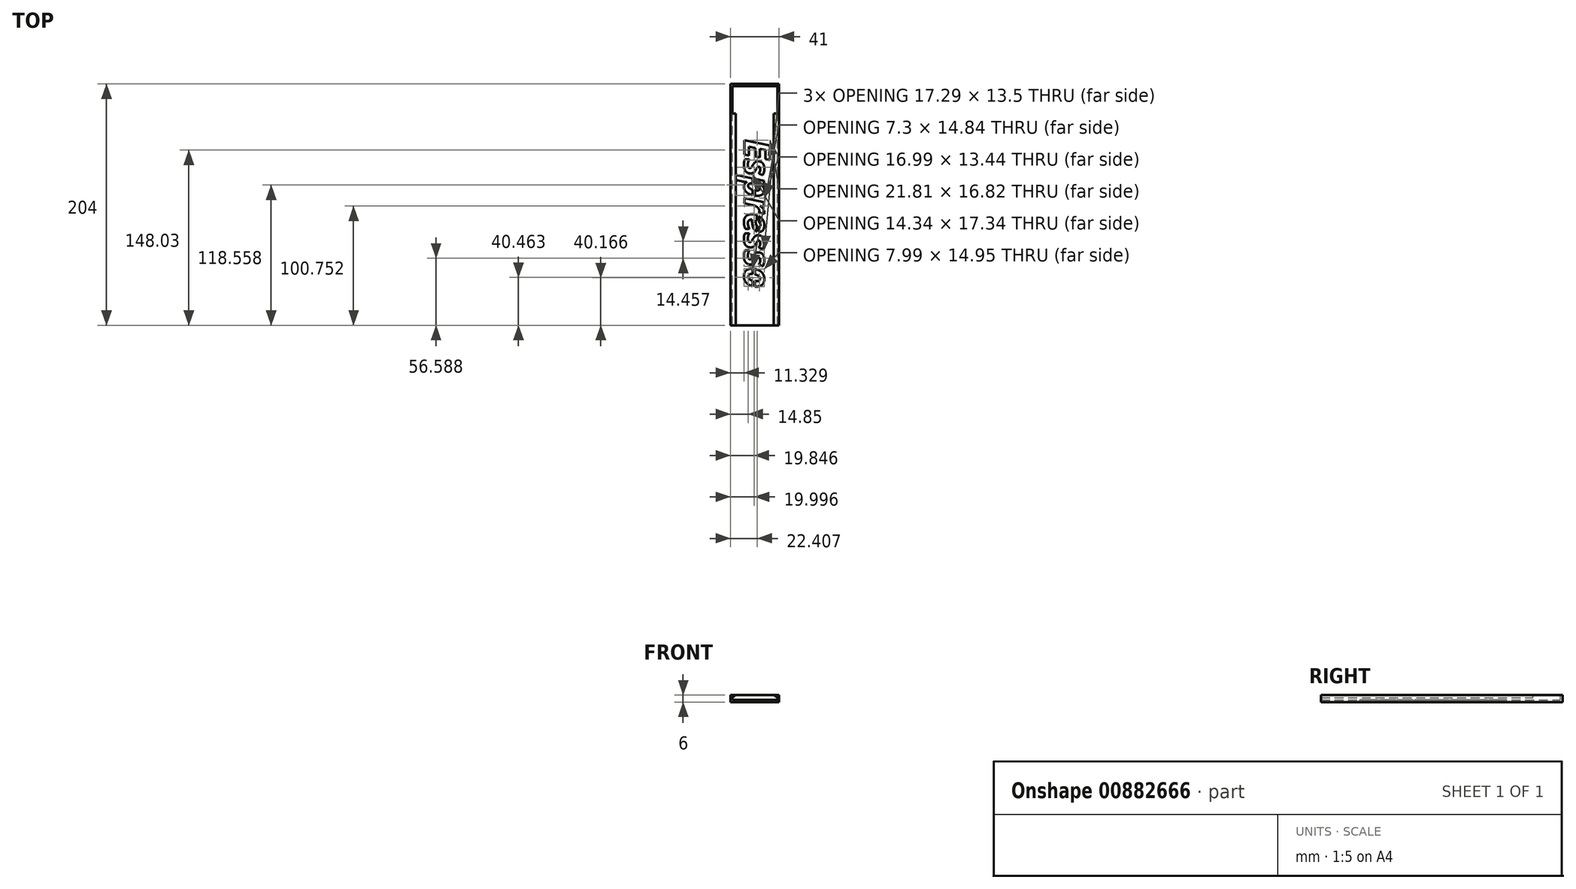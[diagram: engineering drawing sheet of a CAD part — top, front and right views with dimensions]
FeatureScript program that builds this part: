
annotation { "Feature Type Name" : "Feature", "Feature Type Description" : "" }
export const myFeature = defineFeature(function(context is Context, id is Id, definition is map)
    precondition{}
    {
        {
            var Q0;
            Q0=qCreatedBy(makeId("Front.planeOp"),FACE);
            var sketch = newSketch(context, id + "F0", { "sketchPlane" : qUnion([Q0])});
            skLineSegment(sketch, "E0", {"start": v(-20.5, 0) * mm, "end": v(20.5, 0) * mm});
            skLineSegment(sketch, "E1", {"start": v(20.5, 0) * mm, "end": v(20.5, 6) * mm});
            skLineSegment(sketch, "E2", {"start": v(20.5, 6) * mm, "end": v(16, 6) * mm});
            skLineSegment(sketch, "E3", {"start": v(19, 2) * mm, "end": v(-19, 2) * mm});
            skLineSegment(sketch, "E4", {"start": v(-16, 6) * mm, "end": v(-20.5, 6) * mm});
            skLineSegment(sketch, "E5", {"start": v(-20.5, 6) * mm, "end": v(-20.5, 0) * mm});
            skLineSegment(sketch, "E6", {"start": v(-16, 6) * mm, "end": v(16, 6) * mm});
            skLineSegment(sketch, "E7", {"start": v(16, 6) * mm, "end": v(19, 3.6) * mm});
            skLineSegment(sketch, "E8", {"start": v(19, 3.6) * mm, "end": v(19, 2) * mm});
            skLineSegment(sketch, "E9", {"start": v(-16, 6) * mm, "end": v(-19, 3.6) * mm});
            skLineSegment(sketch, "E10", {"start": v(-19, 3.6) * mm, "end": v(-19, 2) * mm});
            skSolve(sketch);
        }
        {
            var Q0;
            Q0=makeQuery(id+"F0.imprint","IMPRINT",FACE,{"disambiguationData":[TD([[makeQuery(id+"F0.imprint","IMPRINT",EDGE,{"derivedFrom":sQuery(id+"F0.wireOp",EDGE,"E0")}),1.0]])]});
            extrude(context, id + "F1", {"entities" : qUnion([Q0]), "depth" : 202 * mm, "offsetDistance" : 25 * mm});
        }
        {
            var Q0;
            Q0=qCreatedBy(makeId("Front.planeOp"),FACE);
            var sketch = newSketch(context, id + "F2", { "sketchPlane" : qUnion([Q0])});
            skLineSegment(sketch, "E11.bottom", {"start": v(20.5, 6) * mm, "end": v(-20.5, 6) * mm});
            skLineSegment(sketch, "E11.top", {"start": v(20.5, 0) * mm, "end": v(-20.5, 0) * mm});
            skLineSegment(sketch, "E11.left", {"start": v(20.5, 6) * mm, "end": v(20.5, 0) * mm});
            skLineSegment(sketch, "E11.right", {"start": v(-20.5, 6) * mm, "end": v(-20.5, 0) * mm});
            skSolve(sketch);
        }
        {
            var Q0;
            Q0=makeQuery(id+"F2.imprint","IMPRINT",FACE,{"disambiguationData":[TD([[makeQuery(id+"F2.imprint","IMPRINT",EDGE,{"derivedFrom":sQuery(id+"F2.wireOp",EDGE,"E11.bottom")}),1.0]])]});
            extrude(context, id + "F3", {"entities" : qUnion([Q0]), "operationType" : NewBodyOperationType.ADD, "oppositeDirection" : true, "depth" : 2 * mm, "offsetDistance" : 25 * mm});
        }
        {
            var Q0;
            Q0=makeQuery(id+"F3.boolean.opBoolean","MERGE",FACE,{"derivedFrom":[makeQuery(id+"F1.opExtrude","SWEPT_FACE",FACE,{"disambiguationData":[OSD([sQuery(id+"F0.wireOp",EDGE,"E2")])]}),makeQuery(id+"F1.opExtrude","SWEPT_FACE",FACE,{"disambiguationData":[OSD([sQuery(id+"F0.wireOp",EDGE,"E4")])]}),makeQuery(id+"F3.opExtrude","SWEPT_FACE",FACE,{"disambiguationData":[OSD([sQuery(id+"F2.wireOp",EDGE,"E11.bottom")])]})]});
            cPlane(context, id + "F4", {"entities" : qUnion([Q0]), "cplaneType" : CPlaneType.OFFSET, "offset" : 0 * mm, "width" : 150 * mm, "height" : 150 * mm});
        }
        {
            var Q0;
            Q0=qCreatedBy(id+"F4.planeOp",FACE);
            var sketch = newSketch(context, id + "F5", { "sketchPlane" : qUnion([Q0])});
            skLineSegment(sketch, "E12.bottom", {"start": v(19, 0) * mm, "end": v(-19, 0) * mm});
            skLineSegment(sketch, "E12.top", {"start": v(19, -23) * mm, "end": v(-19, -23) * mm});
            skLineSegment(sketch, "E12.left", {"start": v(19, 0) * mm, "end": v(19, -23) * mm});
            skLineSegment(sketch, "E12.right", {"start": v(-19, 0) * mm, "end": v(-19, -23) * mm});
            skSolve(sketch);
        }
        {
            var Q0;
            Q0=makeQuery(id+"F5.imprint","IMPRINT",FACE,{"disambiguationData":[TD([[makeQuery(id+"F5.imprint","IMPRINT",EDGE,{"derivedFrom":sQuery(id+"F5.wireOp",EDGE,"E12.bottom")}),1.0]])]});
            extrude(context, id + "F6", {"entities" : qUnion([Q0]), "operationType" : NewBodyOperationType.REMOVE, "oppositeDirection" : true, "depth" : 4 * mm, "offsetDistance" : 25 * mm});
        }
        {
            var Q0;
            Q0=qCreatedBy(id+"F4.planeOp",FACE);
            cPlane(context, id + "F7", {"entities" : qUnion([Q0]), "cplaneType" : CPlaneType.OFFSET, "offset" : 4 * mm, "oppositeDirection" : true, "width" : 150 * mm, "height" : 150 * mm});
        }
        {
            var Q0;
            Q0=qCreatedBy(id+"F7.planeOp",FACE);
            var sketch = newSketch(context, id + "F8", { "sketchPlane" : qUnion([Q0])});
            skText(sketch, "E13", { "text": "Espresso", "fontName": "OpenSans-BoldItalic.ttf"});
            skLineSegment(sketch, "E14.bottom", {"start": v(0, -77.1) * mm, "end": v(-2, -77.1) * mm});
            skLineSegment(sketch, "E14.top", {"start": v(0, -170.14) * mm, "end": v(-2, -170.14) * mm});
            skLineSegment(sketch, "E14.left", {"start": v(0, -77.1) * mm, "end": v(0, -92.85) * mm});
            skLineSegment(sketch, "E14.right", {"start": v(-2, -77.1) * mm, "end": v(-2, -92.85) * mm});
            skLineSegment(sketch, "E15", {"start": v(0, -150.67) * mm, "end": v(0, -170.14) * mm});
            skLineSegment(sketch, "E16", {"start": v(-2, -150.67) * mm, "end": v(-2, -170.14) * mm});
            skLineSegment(sketch, "E17", {"start": v(0, -92.85) * mm, "end": v(-2, -92.85) * mm});
            skLineSegment(sketch, "E18", {"start": v(0, -150.67) * mm, "end": v(-2, -150.67) * mm});
            skLineSegment(sketch, "E19.bottom", {"start": v(3.51, -108.67) * mm, "end": v(1.51, -108.67) * mm});
            skLineSegment(sketch, "E19.top", {"start": v(3.51, -123.94) * mm, "end": v(1.51, -123.94) * mm});
            skLineSegment(sketch, "E19.left", {"start": v(3.51, -108.67) * mm, "end": v(3.51, -123.94) * mm});
            skLineSegment(sketch, "E19.right", {"start": v(1.51, -108.67) * mm, "end": v(1.51, -123.94) * mm});
            const initialGuessF8  = {"E13": [-0.009, -0.04477, 0, -1, 0.022]};
            skSetInitialGuess(sketch, initialGuessF8);
            skSolve(sketch);
        }
        {
            var Q0;
            Q0=makeQuery(id+"F8.imprint","IMPRINT",FACE,{"disambiguationData":[TD([[makeQuery(id+"F8.imprint","IMPRINT",EDGE,{"derivedFrom":sQuery(id+"F8.wireOp",EDGE,"E13.sketch_text.stroke-0")}),-1.0]])]});
            var Q1;
            Q1=makeQuery(id+"F8.imprint","IMPRINT",FACE,{"disambiguationData":[TD([[makeQuery(id+"F8.imprint","IMPRINT",EDGE,{"derivedFrom":sQuery(id+"F8.wireOp",EDGE,"E13.sketch_text.stroke-12")}),-1.0]])]});
            var Q2;
            Q2=makeQuery(id+"F8.imprint","IMPRINT",FACE,{"disambiguationData":[TD([[makeQuery(id+"F8.imprint","IMPRINT",EDGE,{"derivedFrom":sQuery(id+"F8.wireOp",EDGE,"E13.sketch_text.stroke-35")}),-1.0]])]});
            var Q3;
            {var subQ4=sQuery(id+"F8.wireOp",EDGE,"E13.sketch_text.stroke-38");Q3=makeQuery(id+"F8.imprint","IMPRINT",FACE,{"disambiguationData":[TD([[makeQuery(id+"F8.imprint","IMPRINT",EDGE,{"derivedFrom":subQ4}),-1.0]])]});}
            var Q4;
            Q4=makeQuery(id+"F8.imprint","IMPRINT",FACE,{"disambiguationData":[TD([[makeQuery(id+"F8.imprint","IMPRINT",EDGE,{"derivedFrom":sQuery(id+"F8.wireOp",EDGE,"E13.sketch_text.stroke-60")}),-1.0]])]});
            var Q5;
            {var subQ11=sQuery(id+"F8.wireOp",EDGE,"E13.sketch_text.stroke-74");Q5=makeQuery(id+"F8.imprint","IMPRINT",FACE,{"disambiguationData":[TD([[makeQuery(id+"F8.imprint","IMPRINT",EDGE,{"derivedFrom":subQ11}),-1.0]])]});}
            var Q6;
            {var subQ1=sQuery(id+"F8.wireOp",EDGE,"E13.sketch_text.stroke-72");Q6=makeQuery(id+"F8.imprint","IMPRINT",FACE,{"disambiguationData":[TD([[makeQuery(id+"F8.imprint","IMPRINT",EDGE,{"derivedFrom":subQ1}),-1.0]])]});}
            var Q7;
            Q7=makeQuery(id+"F8.imprint","IMPRINT",FACE,{"disambiguationData":[TD([[makeQuery(id+"F8.imprint","IMPRINT",EDGE,{"derivedFrom":sQuery(id+"F8.wireOp",EDGE,"E13.sketch_text.stroke-96")}),-1.0]])]});
            var Q8;
            Q8=makeQuery(id+"F8.imprint","IMPRINT",FACE,{"disambiguationData":[TD([[makeQuery(id+"F8.imprint","IMPRINT",EDGE,{"derivedFrom":sQuery(id+"F8.wireOp",EDGE,"E13.sketch_text.stroke-119")}),-1.0]])]});
            var Q9;
            {var subQ7=sQuery(id+"F8.wireOp",EDGE,"E13.sketch_text.stroke-146");Q9=makeQuery(id+"F8.imprint","IMPRINT",FACE,{"disambiguationData":[TD([[makeQuery(id+"F8.imprint","IMPRINT",EDGE,{"derivedFrom":subQ7}),-1.0]])]});}
            var Q10;
            {var subQ5=sQuery(id+"F8.wireOp",EDGE,"E13.sketch_text.stroke-142");Q10=makeQuery(id+"F8.imprint","IMPRINT",FACE,{"disambiguationData":[TD([[makeQuery(id+"F8.imprint","IMPRINT",EDGE,{"derivedFrom":subQ5}),-1.0]])]});}
            var Q11;
            Q11=makeQuery(id+"F3.boolean.opBoolean","MERGE",FACE,{"derivedFrom":[makeQuery(id+"F1.opExtrude","SWEPT_FACE",FACE,{"disambiguationData":[OSD([sQuery(id+"F0.wireOp",EDGE,"E0")])]}),makeQuery(id+"F3.opExtrude","SWEPT_FACE",FACE,{"disambiguationData":[OSD([sQuery(id+"F2.wireOp",EDGE,"E11.top")])]})]});
            extrude(context, id + "F9", {"entities" : qUnion([Q0, Q1, Q2, Q3, Q4, Q5, Q6, Q7, Q8, Q9, Q10]), "operationType" : NewBodyOperationType.REMOVE, "endBound" : BoundingType.UP_TO_SURFACE, "oppositeDirection" : true, "depth" : 25 * mm, "endBoundEntityFace" : qUnion([Q11]), "offsetDistance" : 25 * mm});
        }
    });
